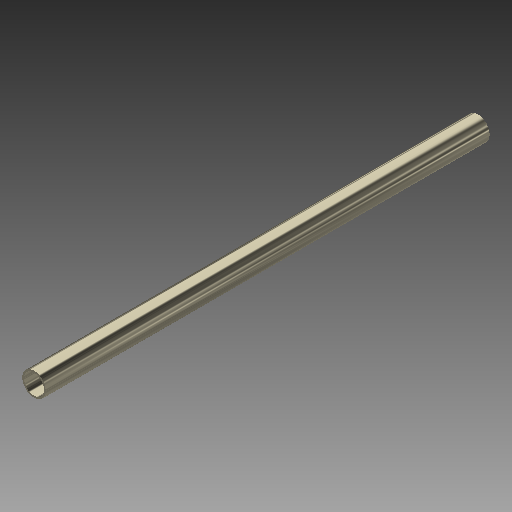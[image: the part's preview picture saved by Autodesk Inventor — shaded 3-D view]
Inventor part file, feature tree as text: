
AUTODESK INVENTOR PART (.ipt)
format: ipt  version: 2019 (Build 230136000, 136)  size: 99,840 bytes
history: native  units: mm
features: extrude x1, sketch x1
ambient origin geometry x8: Origin, YZ Plane, XZ Plane, XY Plane, X Axis, Y Axis, Z Axis, Center Point
bodies: Solid1 (feature_tree)
feature tree (2):
  extrude  "Extrusion1"  Depth=395.5mm
  sketch  "Sketch1"  dims[d0=18.0mm d1=21.0mm d2=395.5mm d3=0.0mm]
